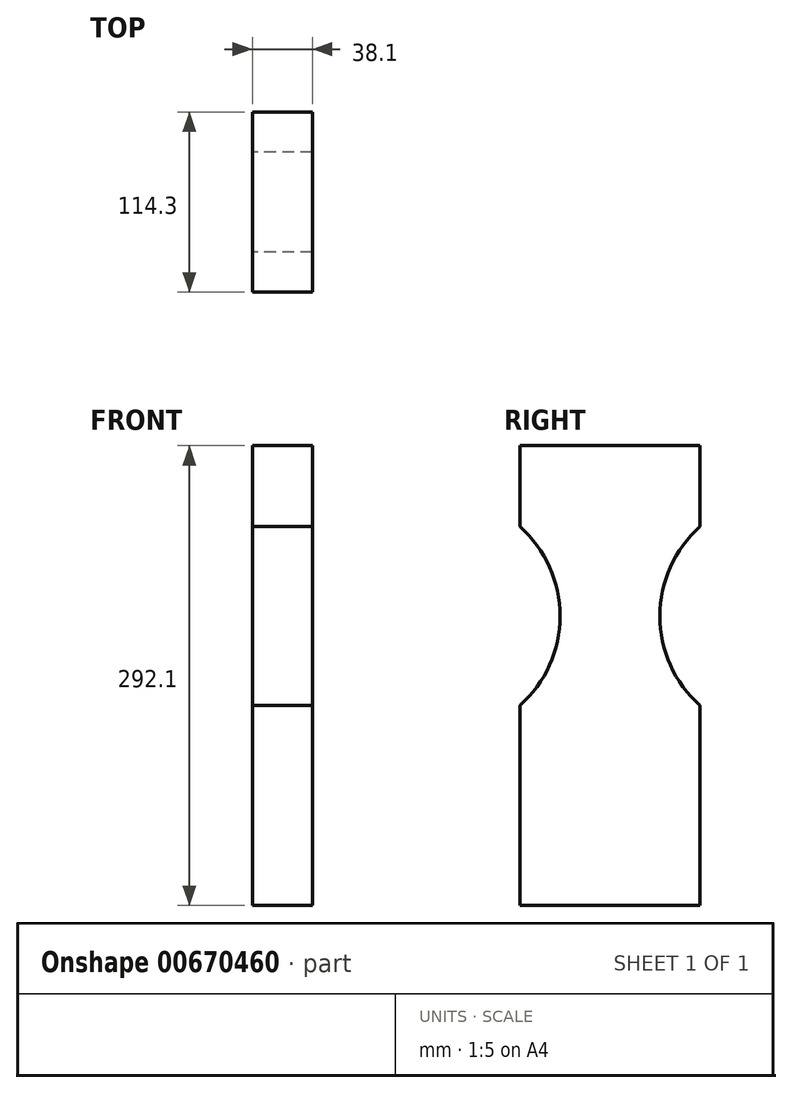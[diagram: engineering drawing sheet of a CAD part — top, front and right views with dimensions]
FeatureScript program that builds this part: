
annotation { "Feature Type Name" : "Feature", "Feature Type Description" : "" }
export const myFeature = defineFeature(function(context is Context, id is Id, definition is map)
    precondition{}
    {
        {
            var Q0;
            Q0=qCreatedBy(makeId("Right.planeOp"),FACE);
            var sketch = newSketch(context, id + "F0", { "sketchPlane" : qUnion([Q0])});
            skLineSegment(sketch, "E0.bottom", {"start": v(0, 0) * mm, "end": v(-114.3, 0) * mm});
            skLineSegment(sketch, "E0.top", {"start": v(0, 292.1) * mm, "end": v(-114.3, 292.1) * mm});
            skLineSegment(sketch, "E0.left", {"start": v(0, 0) * mm, "end": v(0, 127) * mm});
            skLineSegment(sketch, "E0.right", {"start": v(-114.3, 0) * mm, "end": v(-114.3, 127) * mm});
            skArc(sketch, "E1", {"start": v(-114.3, 127) * mm, "mid": v(-88.9, 183.8) * mm, "end": v(-114.3, 240.6) * mm});
            skLineSegment(sketch, "E2", {"start": v(-57.15, 292.1) * mm, "end": v(-57.15, 0) * mm, "construction": true});
            skArc(sketch, "E3.MirrorCS", {"start": v(0, 127) * mm, "mid": v(-25.4, 183.8) * mm, "end": v(0, 240.6) * mm});
            skLineSegment(sketch, "E4.trimOffspring", {"start": v(-114.3, 240.6) * mm, "end": v(-114.3, 292.1) * mm});
            skLineSegment(sketch, "E5.trimOffspring", {"start": v(0, 240.6) * mm, "end": v(0, 292.1) * mm});
            skSolve(sketch);
        }
        {
            var Q0;
            Q0=makeQuery(id+"F0.imprint","IMPRINT",FACE,{"disambiguationData":[TD([[makeQuery(id+"F0.imprint","IMPRINT",EDGE,{"derivedFrom":sQuery(id+"F0.wireOp",EDGE,"E0.bottom")}),-1.0]])]});
            extrude(context, id + "F1", {"entities" : qUnion([Q0]), "depth" : 38.1 * mm, "offsetDistance" : 25.4 * mm});
        }
    });
